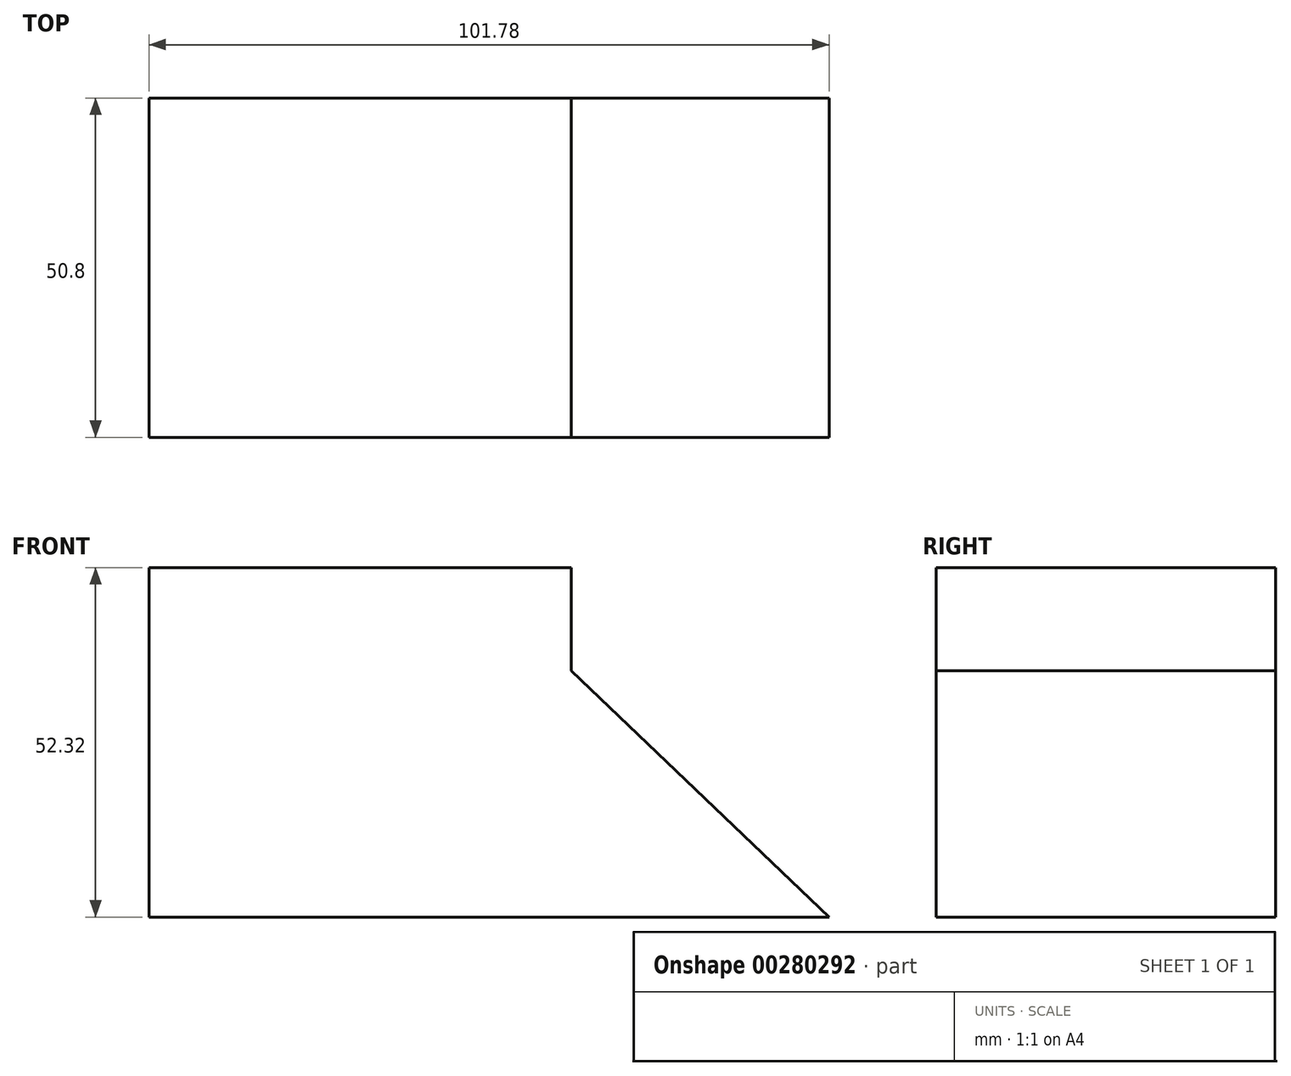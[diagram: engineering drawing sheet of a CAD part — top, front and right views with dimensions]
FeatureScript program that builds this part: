
annotation { "Feature Type Name" : "Feature", "Feature Type Description" : "" }
export const myFeature = defineFeature(function(context is Context, id is Id, definition is map)
    precondition{}
    {
        {
            var Q0;
            Q0=qCreatedBy(makeId("Front.planeOp"),FACE);
            var sketch = newSketch(context, id + "F0", { "sketchPlane" : qUnion([Q0])});
            skLineSegment(sketch, "E0.bottom", {"start": v(-63.2, 52.32) * mm, "end": v(0, 52.32) * mm});
            skLineSegment(sketch, "E0.top", {"start": v(-63.2, 0) * mm, "end": v(0, 0) * mm});
            skLineSegment(sketch, "E0.left", {"start": v(-63.2, 52.32) * mm, "end": v(-63.2, 0) * mm});
            skLineSegment(sketch, "E0.right", {"start": v(0, 52.32) * mm, "end": v(0, 0) * mm});
            skLineSegment(sketch, "E1", {"start": v(0, 36.85) * mm, "end": v(38.57, 0) * mm});
            skLineSegment(sketch, "E2", {"start": v(38.57, 0) * mm, "end": v(0, 0) * mm});
            skSolve(sketch);
        }
        {
            var Q0;
            Q0 = qSketchRegion(id + "F0", true);
            extrude(context, id + "F1", {"entities" : qUnion([Q0]), "depth" : 50.8 * mm});
        }
    });
